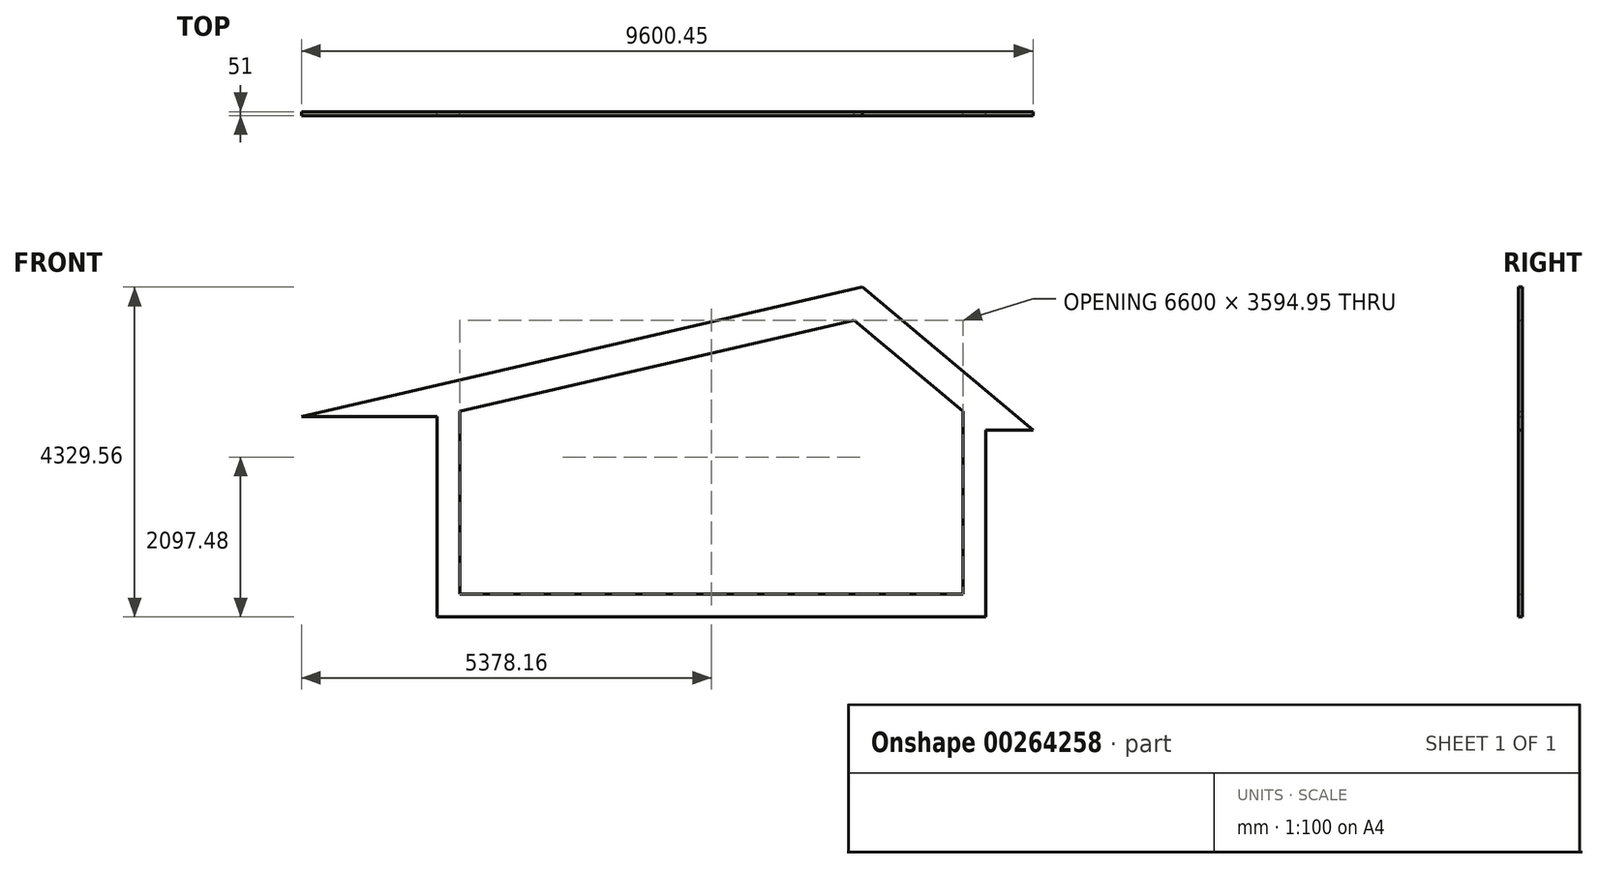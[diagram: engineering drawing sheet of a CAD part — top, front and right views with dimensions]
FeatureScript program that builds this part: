
annotation { "Feature Type Name" : "Feature", "Feature Type Description" : "" }
export const myFeature = defineFeature(function(context is Context, id is Id, definition is map)
    precondition{}
    {
        {
            var Q0;
            Q0=qCreatedBy(makeId("Front.planeOp"),FACE);
            var sketch = newSketch(context, id + "F0", { "sketchPlane" : qUnion([Q0])});
            skLineSegment(sketch, "E0", {"start": v(0, 0) * mm, "end": v(7200, 0) * mm});
            skLineSegment(sketch, "E1", {"start": v(7200, 0) * mm, "end": v(7200, 2148.27) * mm});
            skLineSegment(sketch, "E2", {"start": v(5475.91, 3594.95) * mm, "end": v(7200, 2148.27) * mm});
            skLineSegment(sketch, "E3", {"start": v(5580.25, 4029.56) * mm, "end": v(7822.29, 2148.27) * mm});
            skLineSegment(sketch, "E4", {"start": v(7822.29, 2148.27) * mm, "end": v(7200, 2148.27) * mm});
            skLineSegment(sketch, "E5", {"start": v(6900, 0) * mm, "end": v(6900, 2400) * mm});
            skLineSegment(sketch, "E6", {"start": v(300, 0) * mm, "end": v(300, 2400) * mm});
            skLineSegment(sketch, "E7.top", {"start": v(0, -300) * mm, "end": v(7200, -300) * mm});
            skLineSegment(sketch, "E7.left", {"start": v(0, 0) * mm, "end": v(0, -300) * mm});
            skLineSegment(sketch, "E7.right", {"start": v(7200, 0) * mm, "end": v(7200, -300) * mm});
            skPoint(sketch, "E8.orphan", {"position": v(-2157.86, 2148.27) * mm});
            skLineSegment(sketch, "E9", {"start": v(0, 0) * mm, "end": v(0, 2330.74) * mm});
            skLineSegment(sketch, "E10", {"start": v(300, 2400) * mm, "end": v(5475.91, 3594.95) * mm});
            skLineSegment(sketch, "E11", {"start": v(5580.25, 4029.56) * mm, "end": v(-1778.16, 2330.74) * mm});
            skLineSegment(sketch, "E12", {"start": v(300, 2400) * mm, "end": v(0, 2330.74) * mm});
            skLineSegment(sketch, "E13", {"start": v(0, 2330.74) * mm, "end": v(-1778.16, 2330.74) * mm});
            skSolve(sketch);
        }
        {
            var Q0;
            {var subQ0=sQuery(id+"F0.wireOp",EDGE,"E1");Q0=makeQuery(id+"F0.imprint","IMPRINT",FACE,{"disambiguationData":[TD([[makeQuery(id+"F0.imprint","IMPRINT",EDGE,{"derivedFrom":subQ0}),1.0]])]});}
            var Q1;
            {var subQ0=sQuery(id+"F0.wireOp",EDGE,"8EqBYYlo-JN6x-9FZ1-xOGW-Q1bG1lLWIitg");Q1=makeQuery(id+"F0.imprint","IMPRINT",FACE,{"disambiguationData":[TD([[makeQuery(id+"F0.imprint","IMPRINT",EDGE,{"derivedFrom":subQ0}),-1.0]])]});}
            var Q2;
            Q2=makeQuery(id+"F0.imprint","IMPRINT",FACE,{"disambiguationData":[TD([[makeQuery(id+"F0.imprint","IMPRINT",EDGE,{"derivedFrom":sQuery(id+"F0.wireOp",EDGE,"E3")}),-1.0]])]});
            var Q3;
            Q3=makeQuery(id+"F0.imprint","IMPRINT",FACE,{"disambiguationData":[TD([[makeQuery(id+"F0.imprint","IMPRINT",EDGE,{"derivedFrom":sQuery(id+"F0.wireOp",EDGE,"E7.top")}),1.0]])]});
            var Q4;
            Q4=makeQuery(id+"F0.imprint","IMPRINT",FACE,{"disambiguationData":[TD([[makeQuery(id+"F0.imprint","IMPRINT",EDGE,{"derivedFrom":sQuery(id+"F0.wireOp",EDGE,"cwMlWAMy-VDqT-fIIM-7MTP-BqMpQmSoxAna")}),1.0]])]});
            var Q5;
            {var subQ0=sQuery(id+"F0.wireOp",EDGE,"E6");Q5=makeQuery(id+"F0.imprint","IMPRINT",FACE,{"disambiguationData":[TD([[makeQuery(id+"F0.imprint","IMPRINT",EDGE,{"derivedFrom":subQ0}),1.0]])]});}
            extrude(context, id + "F1", {"entities" : qUnion([Q0, Q1, Q2, Q3, Q4, Q5]), "depth" : 51 * mm, "offsetDistance" : 25 * mm});
        }
        {
            var Q0;
            Q0=makeQuery(id+"F1.opExtrude","CAP_FACE",FACE,{"disambiguationData":[OSD([sQuery(id+"F0.wireOp",EDGE,"E1"),sQuery(id+"F0.wireOp",EDGE,"8EqBYYlo-JN6x-9FZ1-xOGW-Q1bG1lLWIitg"),sQuery(id+"F0.wireOp",EDGE,"QXYJRDg6-itMc-f0Yr-3ZXk-JT26ID68Id6O"),sQuery(id+"F0.wireOp",EDGE,"E2"),sQuery(id+"F0.wireOp",EDGE,"cwMlWAMy-VDqT-fIIM-7MTP-BqMpQmSoxAna"),sQuery(id+"F0.wireOp",EDGE,"qtnertt5-nrUa-avFc-CJxP-4AKEBYPfvtiK"),sQuery(id+"F0.wireOp",EDGE,"E3"),sQuery(id+"F0.wireOp",EDGE,"E4"),sQuery(id+"F0.wireOp",EDGE,"E5"),sQuery(id+"F0.wireOp",EDGE,"E6"),sQuery(id+"F0.wireOp",EDGE,"E0"),sQuery(id+"F0.wireOp",EDGE,"E7.top"),sQuery(id+"F0.wireOp",EDGE,"E7.left"),sQuery(id+"F0.wireOp",EDGE,"E7.right"),sQuery(id+"F0.wireOp",EDGE,"EAvVDQcS-22Rc-9MP5-1QEV-ONJTxwhVlQMO")])],"isStart":false});
            var sketch = newSketch(context, id + "F2", { "sketchPlane" : qUnion([Q0])});
            skLineSegment(sketch, "E14.0", {"start": v(11, 2947.71) * mm, "end": v(11, -289) * mm});
            skLineSegment(sketch, "E14.1", {"start": v(-575.6, 2947.71) * mm, "end": v(11, 2947.71) * mm});
            skLineSegment(sketch, "E14.2", {"start": v(11, -289) * mm, "end": v(7189, -289) * mm});
            skLineSegment(sketch, "E14.3", {"start": v(-575.6, 3020.85) * mm, "end": v(-575.6, 2947.71) * mm});
            skLineSegment(sketch, "E14.4", {"start": v(7189, -289) * mm, "end": v(7189, 2159.27) * mm});
            skLineSegment(sketch, "E14.5", {"start": v(7189, 2159.27) * mm, "end": v(7792.07, 2159.27) * mm});
            skLineSegment(sketch, "E14.6", {"start": v(7792.07, 2159.27) * mm, "end": v(4988.5, 4511.74) * mm});
            skLineSegment(sketch, "E14.7", {"start": v(4988.5, 4511.74) * mm, "end": v(-575.6, 3020.85) * mm});
            skLineSegment(sketch, "E15.0", {"start": v(4262.13, 3353.42) * mm, "end": v(5111, 2504.56) * mm});
            skLineSegment(sketch, "E15.1", {"start": v(289, 2288.83) * mm, "end": v(4262.13, 3353.42) * mm});
            skLineSegment(sketch, "E15.2", {"start": v(5111, -11) * mm, "end": v(5111, 2504.56) * mm});
            skLineSegment(sketch, "E15.3", {"start": v(289, -11) * mm, "end": v(5111, -11) * mm});
            skLineSegment(sketch, "E15.4", {"start": v(289, -11) * mm, "end": v(289, 2288.83) * mm});
            skLineSegment(sketch, "E16.0", {"start": v(-5, 2931.17) * mm, "end": v(-5, -305) * mm});
            skLineSegment(sketch, "E16.1", {"start": v(-592.1, 2931.17) * mm, "end": v(-5, 2931.17) * mm});
            skLineSegment(sketch, "E16.2", {"start": v(-5, -305) * mm, "end": v(7205, -305) * mm});
            skLineSegment(sketch, "E16.3", {"start": v(-592.1, 3032.58) * mm, "end": v(-592.1, 2931.17) * mm});
            skLineSegment(sketch, "E16.4", {"start": v(7205, -305) * mm, "end": v(7205, 2143.27) * mm});
            skLineSegment(sketch, "E16.5", {"start": v(7205, 2143.27) * mm, "end": v(7836.03, 2143.27) * mm});
            skLineSegment(sketch, "E16.6", {"start": v(7836.03, 2143.27) * mm, "end": v(4992.78, 4529.04) * mm});
            skLineSegment(sketch, "E16.7", {"start": v(4992.78, 4529.04) * mm, "end": v(-592.1, 3032.58) * mm});
            skSolve(sketch);
        }
        {
            var Q0;
            Q0=makeQuery(id+"F2.imprint","IMPRINT",FACE,{"disambiguationData":[TD([[makeQuery(id+"F2.imprint","IMPRINT",EDGE,{"derivedFrom":sQuery(id+"F2.wireOp",EDGE,"E14.0")}),1.0]])]});
            extrude(context, id + "F3", {"entities" : qUnion([Q0]), "operationType" : NewBodyOperationType.REMOVE, "endBound" : BoundingType.THROUGH_ALL, "oppositeDirection" : true, "depth" : 25 * mm});
        }
    });
